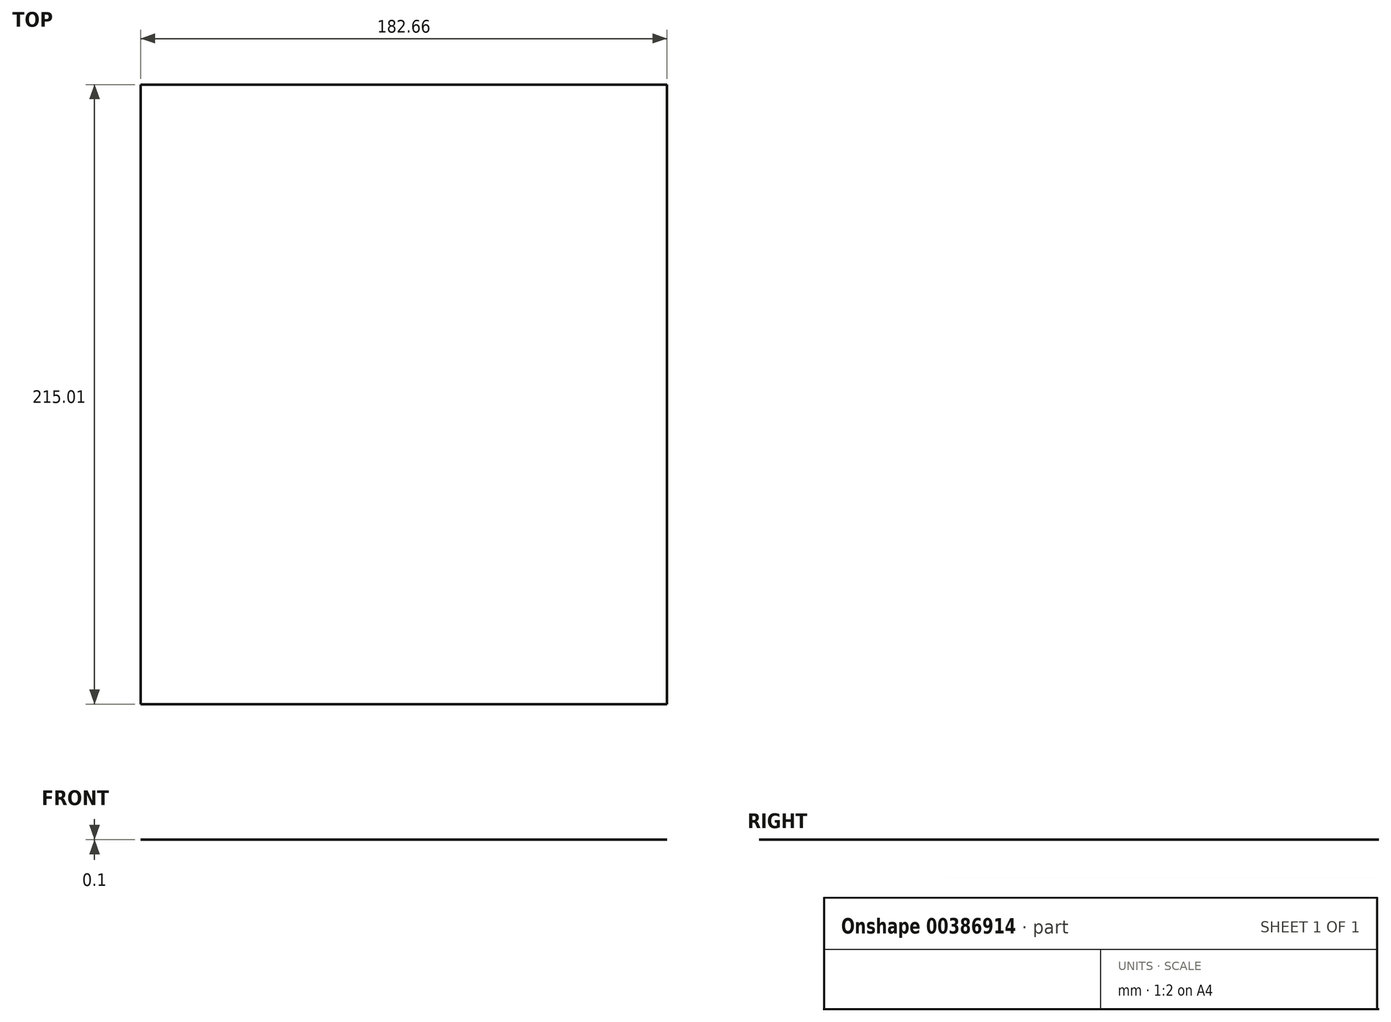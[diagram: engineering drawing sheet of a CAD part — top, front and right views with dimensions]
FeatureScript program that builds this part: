
annotation { "Feature Type Name" : "Feature", "Feature Type Description" : "" }
export const myFeature = defineFeature(function(context is Context, id is Id, definition is map)
    precondition{}
    {
        {
            var Q0;
            Q0=qCreatedBy(makeId("Top.planeOp"),FACE);
            cPlane(context, id + "F0", {"entities" : qUnion([Q0]), "cplaneType" : CPlaneType.OFFSET, "offset" : 115 * mm, "oppositeDirection" : true, "width" : 150 * mm, "height" : 150 * mm});
        }
        {
            var Q0;
            Q0=qCreatedBy(id+"F0.planeOp",FACE);
            var sketch = newSketch(context, id + "F1", { "sketchPlane" : qUnion([Q0])});
            skLineSegment(sketch, "E0.bottom", {"start": v(0, 0) * mm, "end": v(182.66, 0) * mm});
            skLineSegment(sketch, "E0.top", {"start": v(0, 215) * mm, "end": v(182.66, 215) * mm});
            skLineSegment(sketch, "E0.left", {"start": v(0, 0) * mm, "end": v(0, 215) * mm});
            skLineSegment(sketch, "E0.right", {"start": v(182.66, 0) * mm, "end": v(182.66, 215) * mm});
            skSolve(sketch);
        }
        {
            var Q0;
            Q0 = qSketchRegion(id + "F1", true);
            extrude(context, id + "F2", {"entities" : qUnion([Q0]), "depth" : .1 * mm});
        }
    });
